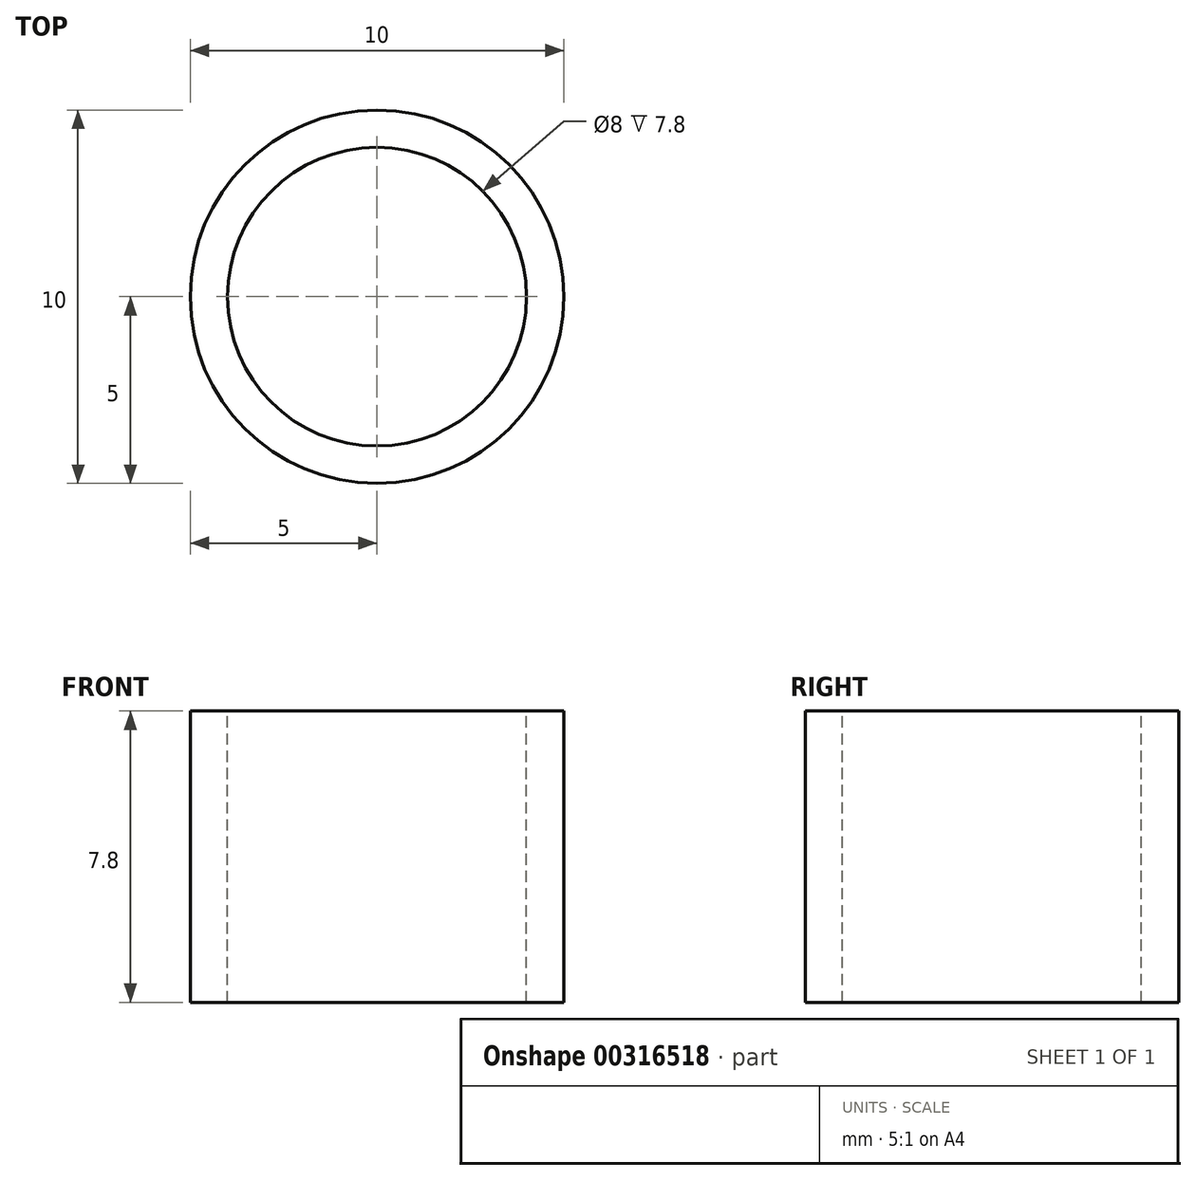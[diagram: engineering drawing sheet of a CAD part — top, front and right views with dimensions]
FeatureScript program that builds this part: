
annotation { "Feature Type Name" : "Feature", "Feature Type Description" : "" }
export const myFeature = defineFeature(function(context is Context, id is Id, definition is map)
    precondition{}
    {
        {
            var Q0;
            Q0=qCreatedBy(makeId("Top.planeOp"),FACE);
            var sketch = newSketch(context, id + "F0", { "sketchPlane" : qUnion([Q0])});
            skCircle(sketch, "E0", {"center": v(0, 0) * mm, "radius": 4 * mm});
            skCircle(sketch, "E1", {"center": v(0, 0) * mm, "radius": 5 * mm});
            skSolve(sketch);
        }
        {
            var Q0;
            Q0=makeQuery(id+"F0.imprint","IMPRINT",FACE,{"disambiguationData":[TD([[makeQuery(id+"F0.imprint","IMPRINT",EDGE,{"derivedFrom":sQuery(id+"F0.wireOp",EDGE,"E0")}),-1.0]])]});
            extrude(context, id + "F1", {"entities" : qUnion([Q0]), "endBound" : BoundingType.SYMMETRIC, "oppositeDirection" : true, "depth" : 7.8 * mm});
        }
    });
